# Revit family: Bathtub-Freestanding-DXV-Seagram-D60545004
name_source: partatom
category: Plumbing Fixtures
revit_build: Autodesk Revit 2014 (Build: 20130308_1515(x64)
units: mm (PartAtom-declared; Revit-internal decimal feet)

## types (1)
- D60545004.415
    Assembly Code = D2010510
    Body Material = Acrylic-DXV-415-Canvas White
    CW Connection = No
    CWFU = 0
    Default Elevation = 0"
    Description = Freestanding Tub With Deck Mount Canvas White
    HW Connection = No
    HWFU = 0
    Height = 22"
    Installation Type = Freestanding
    Length = 36"
    Manufacturer = DXV
    Material = Acrylic-DXV-415-Canvas White
    Model = D60545004.415
    Price = Prices may vary. Please consult Manufacturer Representative for most up-to-date price list.
    Product Documentation Link = https://dxv01.blob.core.windows.net
    Product Page URL = https://www.dxv.com
    URL = www.dxv.com
    Vent Connection = No
    WFU = 0
    Waste Connection = Yes
    Waste Connection Diameter = 1 1/2"
    Waste Connection Radius = 3/4"
    Width = 66"

## geometry (parser evidence)
native form markers: Sweep x3
no freeform markers — native parametric forms only
